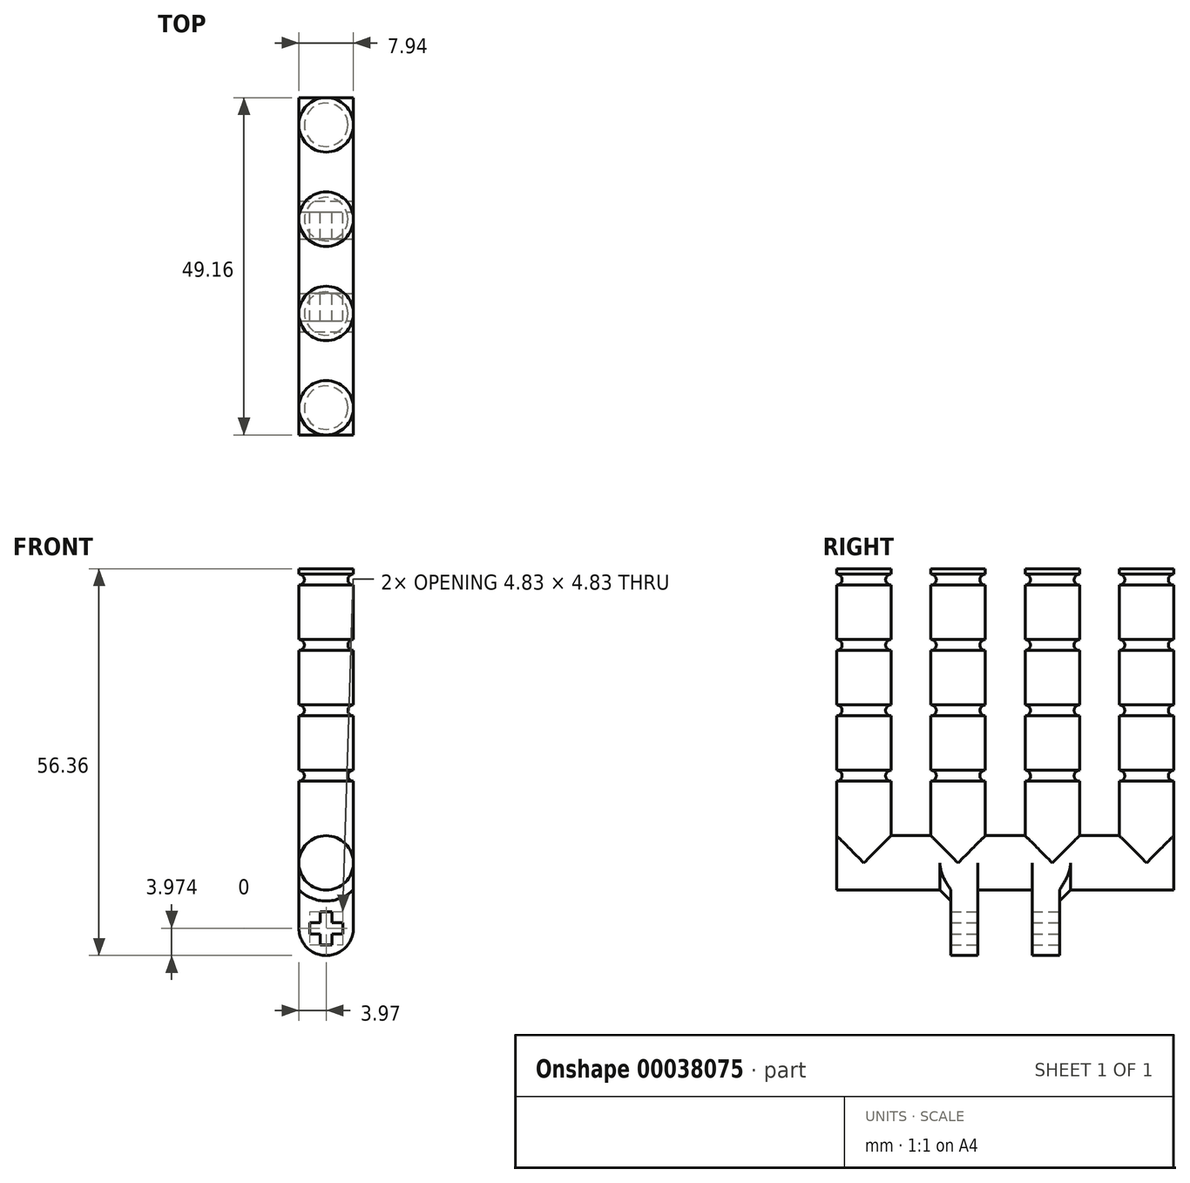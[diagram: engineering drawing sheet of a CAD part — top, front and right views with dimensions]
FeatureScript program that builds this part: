
annotation { "Feature Type Name" : "Feature", "Feature Type Description" : "" }
export const myFeature = defineFeature(function(context is Context, id is Id, definition is map)
    precondition{}
    {
        {
            var Q0;
            Q0=qCreatedBy(makeId("Top.planeOp"),FACE);
            var sketch = newSketch(context, id + "F0", { "sketchPlane" : qUnion([Q0])});
            skLineSegment(sketch, "E0.rect.bottom", {"start": v(3.97, -24.58) * mm, "end": v(-3.97, -24.58) * mm});
            skLineSegment(sketch, "E0.rect.top", {"start": v(3.97, 24.58) * mm, "end": v(-3.97, 24.58) * mm});
            skLineSegment(sketch, "E0.rect.left", {"start": v(3.97, -24.58) * mm, "end": v(3.97, 24.58) * mm});
            skLineSegment(sketch, "E0.rect.right", {"start": v(-3.97, -24.58) * mm, "end": v(-3.97, 24.58) * mm});
            skPoint(sketch, "E0.rect.middle", {"position": v(0, 0) * mm});
            skSolve(sketch);
        }
        {
            var Q0;
            Q0 = qSketchRegion(id + "F0", true);
            extrude(context, id + "F1", {"entities" : qUnion([Q0]), "depth" : 7.94 * mm});
        }
        {
            var Q0;
            Q0=makeQuery(id+"F1.opExtrude","CAP_FACE",FACE,{"disambiguationData":[OSD([sQuery(id+"F0.wireOp",EDGE,"E0.rect.bottom"),sQuery(id+"F0.wireOp",EDGE,"E0.rect.top"),sQuery(id+"F0.wireOp",EDGE,"E0.rect.left"),sQuery(id+"F0.wireOp",EDGE,"E0.rect.right")])],"isStart":false});
            var sketch = newSketch(context, id + "F2", { "sketchPlane" : qUnion([Q0])});
            skLineSegment(sketch, "E1", {"start": v(0, 24.58) * mm, "end": v(0, 20.61) * mm, "construction": true});
            skLineSegment(sketch, "E2", {"start": v(0, 20.61) * mm, "end": v(0, 6.87) * mm, "construction": true});
            skLineSegment(sketch, "E3", {"start": v(0, 6.87) * mm, "end": v(0, -6.87) * mm, "construction": true});
            skLineSegment(sketch, "E4", {"start": v(0, -6.87) * mm, "end": v(0, -20.61) * mm, "construction": true});
            skLineSegment(sketch, "E5", {"start": v(0, -20.61) * mm, "end": v(0, -24.58) * mm, "construction": true});
            skCircle(sketch, "E6", {"center": v(0, 20.61) * mm, "radius": 3.97 * mm});
            skCircle(sketch, "E7", {"center": v(0, -20.61) * mm, "radius": 3.97 * mm});
            skCircle(sketch, "E8", {"center": v(0, -6.87) * mm, "radius": 3.97 * mm});
            skCircle(sketch, "E9", {"center": v(0, 6.87) * mm, "radius": 3.97 * mm});
            skSolve(sketch);
        }
        {
            var Q0;
            Q0 = qSketchRegion(id + "F2", true);
            extrude(context, id + "F3", {"entities" : qUnion([Q0]), "operationType" : NewBodyOperationType.ADD, "depth" : 152.4 * mm});
        }
        {
            var Q0;
            Q0=makeQuery(id+"F1.opExtrude","CAP_FACE",FACE,{"disambiguationData":[OSD([sQuery(id+"F0.wireOp",EDGE,"E0.rect.bottom"),sQuery(id+"F0.wireOp",EDGE,"E0.rect.top"),sQuery(id+"F0.wireOp",EDGE,"E0.rect.left"),sQuery(id+"F0.wireOp",EDGE,"E0.rect.right")])],"isStart":true});
            var sketch = newSketch(context, id + "F4", { "sketchPlane" : qUnion([Q0])});
            skLineSegment(sketch, "E10", {"start": v(3.97, 0) * mm, "end": v(0, 0) * mm, "construction": true});
            skPoint(sketch, "E10.endSnap0", {"position": v(3.97, 0) * mm});
            skLineSegment(sketch, "E11", {"start": v(0, -3.97) * mm, "end": v(0, 3.97) * mm, "construction": true});
            skLineSegment(sketch, "E12.bottom", {"start": v(-3.97, 3.97) * mm, "end": v(3.97, 3.97) * mm});
            skLineSegment(sketch, "E12.top", {"start": v(-3.97, 7.94) * mm, "end": v(3.97, 7.94) * mm});
            skLineSegment(sketch, "E12.left", {"start": v(-3.97, 3.97) * mm, "end": v(-3.97, 7.94) * mm});
            skLineSegment(sketch, "E12.right", {"start": v(3.97, 3.97) * mm, "end": v(3.97, 7.94) * mm});
            skLineSegment(sketch, "E13.bottom", {"start": v(-3.97, -7.94) * mm, "end": v(3.97, -7.94) * mm});
            skLineSegment(sketch, "E13.top", {"start": v(-3.97, -3.97) * mm, "end": v(3.97, -3.97) * mm});
            skLineSegment(sketch, "E13.left", {"start": v(-3.97, -7.94) * mm, "end": v(-3.97, -3.97) * mm});
            skLineSegment(sketch, "E13.right", {"start": v(3.97, -7.94) * mm, "end": v(3.97, -3.97) * mm});
            skSolve(sketch);
        }
        {
            var Q0;
            Q0 = qSketchRegion(id + "F4", true);
            extrude(context, id + "F5", {"entities" : qUnion([Q0]), "operationType" : NewBodyOperationType.ADD, "depth" : 9.52 * mm});
        }
        {
            var Q0;
            Q0=qCreatedBy(makeId("Right.planeOp"),FACE);
            var sketch = newSketch(context, id + "F6", { "sketchPlane" : qUnion([Q0])});
            skLineSegment(sketch, "E14", {"start": v(24.58, 7.94) * mm, "end": v(24.58, 15.88) * mm});
            skLineSegment(sketch, "E15.bottom", {"start": v(24.58, 15.88) * mm, "end": v(23.79, 15.88) * mm});
            skLineSegment(sketch, "E15.top", {"start": v(24.58, 17.46) * mm, "end": v(23.79, 17.46) * mm});
            skLineSegment(sketch, "E15.left", {"start": v(24.58, 15.88) * mm, "end": v(24.58, 17.46) * mm});
            skLineSegment(sketch, "E15.right", {"start": v(23.79, 15.88) * mm, "end": v(23.79, 17.46) * mm, "construction": true});
            skLineSegment(sketch, "E16", {"start": v(24.58, 17.46) * mm, "end": v(24.58, 25.4) * mm, "construction": true});
            skLineSegment(sketch, "E17.bottom", {"start": v(24.58, 25.4) * mm, "end": v(23.79, 25.4) * mm});
            skLineSegment(sketch, "E17.top", {"start": v(24.58, 26.99) * mm, "end": v(23.79, 26.99) * mm});
            skLineSegment(sketch, "E17.left", {"start": v(24.58, 25.4) * mm, "end": v(24.58, 26.99) * mm});
            skLineSegment(sketch, "E17.right", {"start": v(23.79, 25.4) * mm, "end": v(23.79, 26.99) * mm, "construction": true});
            skLineSegment(sketch, "E18.bottom", {"start": v(24.58, 46.04) * mm, "end": v(23.79, 46.04) * mm});
            skLineSegment(sketch, "E18.top", {"start": v(24.58, 44.45) * mm, "end": v(23.79, 44.45) * mm});
            skLineSegment(sketch, "E18.left", {"start": v(24.58, 44.45) * mm, "end": v(24.58, 46.04) * mm});
            skLineSegment(sketch, "E18.right", {"start": v(23.79, 44.45) * mm, "end": v(23.79, 46.04) * mm, "construction": true});
            skLineSegment(sketch, "E19.bottom", {"start": v(24.58, 34.92) * mm, "end": v(23.79, 34.92) * mm});
            skLineSegment(sketch, "E19.top", {"start": v(24.58, 36.51) * mm, "end": v(23.79, 36.51) * mm});
            skLineSegment(sketch, "E19.left", {"start": v(24.58, 34.92) * mm, "end": v(24.58, 36.51) * mm});
            skLineSegment(sketch, "E19.right", {"start": v(23.79, 34.92) * mm, "end": v(23.79, 36.51) * mm, "construction": true});
            skLineSegment(sketch, "E20", {"start": v(24.58, 26.99) * mm, "end": v(24.58, 34.92) * mm, "construction": true});
            skLineSegment(sketch, "E21", {"start": v(24.58, 36.51) * mm, "end": v(24.58, 44.45) * mm, "construction": true});
            skArc(sketch, "E22", {"start": v(24.58, 17.46) * mm, "mid": v(23.79, 16.67) * mm, "end": v(24.58, 15.88) * mm});
            skArc(sketch, "E23", {"start": v(24.58, 26.99) * mm, "mid": v(23.79, 26.2) * mm, "end": v(24.58, 25.4) * mm});
            skArc(sketch, "E24", {"start": v(24.58, 36.51) * mm, "mid": v(23.79, 35.72) * mm, "end": v(24.58, 34.92) * mm});
            skArc(sketch, "E25", {"start": v(24.58, 46.04) * mm, "mid": v(23.79, 45.24) * mm, "end": v(24.58, 44.45) * mm});
            skLineSegment(sketch, "E26", {"start": v(24.58, 46.04) * mm, "end": v(24.58, 46.83) * mm});
            skLineSegment(sketch, "E27.bottom", {"start": v(24.58, 46.83) * mm, "end": v(20.61, 46.83) * mm});
            skLineSegment(sketch, "E27.top", {"start": v(24.58, 160.34) * mm, "end": v(20.61, 160.34) * mm});
            skLineSegment(sketch, "E27.left", {"start": v(24.58, 46.83) * mm, "end": v(24.58, 160.34) * mm});
            skLineSegment(sketch, "E27.right", {"start": v(20.61, 46.83) * mm, "end": v(20.61, 160.34) * mm});
            skSolve(sketch);
        }
        {
            var Q0;
            Q0 = qSketchRegion(id + "F6", true);
            var Q1;
            Q1=makeQuery(id+"F3.opExtrude","CAP_EDGE",EDGE,{"disambiguationData":[OSD([sQuery(id+"F2.wireOp",EDGE,"E6")])],"isStart":false});
            revolve(context, id + "F7", {"operationType" : NewBodyOperationType.REMOVE, "entities" : qUnion([Q0]), "axis" : qUnion([Q1]), "revolveType" : RevolveType.FULL, "oppositeDirection" : true});
        }
        {
            var Q0;
            Q0=qCreatedBy(makeId("Right.planeOp"),FACE);
            var sketch = newSketch(context, id + "F8", { "sketchPlane" : qUnion([Q0])});
            skLineSegment(sketch, "E28", {"start": v(10.84, 7.94) * mm, "end": v(6.87, 7.94) * mm, "construction": true});
            skLineSegment(sketch, "E29", {"start": v(10.84, 7.94) * mm, "end": v(10.84, 15.88) * mm, "construction": true});
            skLineSegment(sketch, "E30.bottom", {"start": v(10.84, 15.88) * mm, "end": v(10.05, 15.88) * mm, "construction": true});
            skLineSegment(sketch, "E30.top", {"start": v(10.84, 17.46) * mm, "end": v(10.05, 17.46) * mm, "construction": true});
            skLineSegment(sketch, "E30.left", {"start": v(10.84, 15.88) * mm, "end": v(10.84, 17.46) * mm});
            skLineSegment(sketch, "E30.right", {"start": v(10.05, 15.88) * mm, "end": v(10.05, 17.46) * mm, "construction": true});
            skLineSegment(sketch, "E31", {"start": v(10.84, 17.46) * mm, "end": v(10.84, 25.4) * mm, "construction": true});
            skLineSegment(sketch, "E32.bottom", {"start": v(10.84, 25.4) * mm, "end": v(10.05, 25.4) * mm, "construction": true});
            skLineSegment(sketch, "E32.top", {"start": v(10.84, 26.99) * mm, "end": v(10.05, 26.99) * mm, "construction": true});
            skLineSegment(sketch, "E32.left", {"start": v(10.84, 25.4) * mm, "end": v(10.84, 26.99) * mm});
            skLineSegment(sketch, "E32.right", {"start": v(10.05, 25.4) * mm, "end": v(10.05, 26.99) * mm, "construction": true});
            skArc(sketch, "E33", {"start": v(10.84, 26.99) * mm, "mid": v(10.05, 26.2) * mm, "end": v(10.84, 25.4) * mm});
            skArc(sketch, "E34", {"start": v(10.84, 17.46) * mm, "mid": v(10.05, 16.67) * mm, "end": v(10.84, 15.88) * mm});
            skLineSegment(sketch, "E35", {"start": v(10.84, 26.99) * mm, "end": v(10.84, 34.93) * mm, "construction": true});
            skLineSegment(sketch, "E36", {"start": v(10.84, 36.51) * mm, "end": v(10.84, 44.45) * mm, "construction": true});
            skLineSegment(sketch, "E37.bottom", {"start": v(10.84, 34.93) * mm, "end": v(10.05, 34.93) * mm, "construction": true});
            skLineSegment(sketch, "E37.top", {"start": v(10.84, 36.51) * mm, "end": v(10.05, 36.51) * mm, "construction": true});
            skLineSegment(sketch, "E37.left", {"start": v(10.84, 34.93) * mm, "end": v(10.84, 36.51) * mm});
            skLineSegment(sketch, "E37.right", {"start": v(10.05, 34.93) * mm, "end": v(10.05, 36.51) * mm, "construction": true});
            skLineSegment(sketch, "E38.bottom", {"start": v(10.84, 44.45) * mm, "end": v(10.05, 44.45) * mm, "construction": true});
            skLineSegment(sketch, "E38.top", {"start": v(10.84, 46.04) * mm, "end": v(10.05, 46.04) * mm, "construction": true});
            skLineSegment(sketch, "E38.left", {"start": v(10.84, 44.45) * mm, "end": v(10.84, 46.04) * mm});
            skLineSegment(sketch, "E38.right", {"start": v(10.05, 44.45) * mm, "end": v(10.05, 46.04) * mm, "construction": true});
            skLineSegment(sketch, "E39", {"start": v(10.84, 46.04) * mm, "end": v(10.84, 46.83) * mm});
            skLineSegment(sketch, "E40.bottom", {"start": v(10.84, 46.83) * mm, "end": v(6.87, 46.83) * mm});
            skLineSegment(sketch, "E40.top", {"start": v(10.84, 160.34) * mm, "end": v(6.87, 160.34) * mm});
            skLineSegment(sketch, "E40.left", {"start": v(10.84, 46.83) * mm, "end": v(10.84, 160.34) * mm});
            skLineSegment(sketch, "E40.right", {"start": v(6.87, 46.83) * mm, "end": v(6.87, 160.34) * mm});
            skArc(sketch, "E41", {"start": v(10.84, 46.04) * mm, "mid": v(10.05, 45.24) * mm, "end": v(10.84, 44.45) * mm});
            skArc(sketch, "E42", {"start": v(10.84, 36.51) * mm, "mid": v(10.05, 35.72) * mm, "end": v(10.84, 34.93) * mm});
            skSolve(sketch);
        }
        {
            var Q0;
            Q0 = qSketchRegion(id + "F8", true);
            var Q1;
            Q1=makeQuery(id+"F3.opExtrude","CAP_EDGE",EDGE,{"disambiguationData":[OSD([sQuery(id+"F2.wireOp",EDGE,"E9")])],"isStart":false});
            revolve(context, id + "F9", {"operationType" : NewBodyOperationType.REMOVE, "entities" : qUnion([Q0]), "axis" : qUnion([Q1]), "revolveType" : RevolveType.FULL, "oppositeDirection" : true});
        }
        {
            var Q0;
            Q0=qCreatedBy(makeId("Right.planeOp"),FACE);
            var sketch = newSketch(context, id + "F10", { "sketchPlane" : qUnion([Q0])});
            skLineSegment(sketch, "E43", {"start": v(-6.87, 7.94) * mm, "end": v(-2.9, 7.94) * mm});
            skLineSegment(sketch, "E44", {"start": v(-2.9, 7.94) * mm, "end": v(-2.9, 15.88) * mm, "construction": true});
            skLineSegment(sketch, "E45.bottom", {"start": v(-2.9, 15.88) * mm, "end": v(-3.7, 15.88) * mm});
            skLineSegment(sketch, "E45.top", {"start": v(-2.9, 17.46) * mm, "end": v(-3.7, 17.46) * mm});
            skLineSegment(sketch, "E45.left", {"start": v(-2.9, 15.88) * mm, "end": v(-2.9, 17.46) * mm});
            skLineSegment(sketch, "E45.right", {"start": v(-3.7, 15.88) * mm, "end": v(-3.7, 17.46) * mm, "construction": true});
            skLineSegment(sketch, "E46", {"start": v(-2.9, 17.46) * mm, "end": v(-2.9, 25.4) * mm, "construction": true});
            skLineSegment(sketch, "E47.bottom", {"start": v(-2.9, 25.4) * mm, "end": v(-3.7, 25.4) * mm});
            skLineSegment(sketch, "E47.top", {"start": v(-2.9, 26.99) * mm, "end": v(-3.7, 26.99) * mm});
            skLineSegment(sketch, "E47.left", {"start": v(-2.9, 25.4) * mm, "end": v(-2.9, 26.99) * mm});
            skLineSegment(sketch, "E47.right", {"start": v(-3.7, 25.4) * mm, "end": v(-3.7, 26.99) * mm, "construction": true});
            skLineSegment(sketch, "E48", {"start": v(-2.9, 26.99) * mm, "end": v(-2.9, 34.93) * mm, "construction": true});
            skLineSegment(sketch, "E49.bottom", {"start": v(-2.9, 34.93) * mm, "end": v(-3.7, 34.93) * mm});
            skLineSegment(sketch, "E49.top", {"start": v(-2.9, 36.51) * mm, "end": v(-3.7, 36.51) * mm, "construction": true});
            skLineSegment(sketch, "E49.left", {"start": v(-2.9, 34.93) * mm, "end": v(-2.9, 36.51) * mm});
            skLineSegment(sketch, "E49.right", {"start": v(-3.7, 34.93) * mm, "end": v(-3.7, 36.51) * mm, "construction": true});
            skLineSegment(sketch, "E50", {"start": v(-2.9, 36.51) * mm, "end": v(-2.9, 44.45) * mm, "construction": true});
            skLineSegment(sketch, "E51.bottom", {"start": v(-2.9, 44.45) * mm, "end": v(-3.7, 44.45) * mm});
            skLineSegment(sketch, "E51.top", {"start": v(-2.9, 46.04) * mm, "end": v(-3.7, 46.04) * mm, "construction": true});
            skLineSegment(sketch, "E51.left", {"start": v(-2.9, 44.45) * mm, "end": v(-2.9, 46.04) * mm});
            skLineSegment(sketch, "E51.right", {"start": v(-3.7, 44.45) * mm, "end": v(-3.7, 46.04) * mm, "construction": true});
            skLineSegment(sketch, "E52", {"start": v(-2.9, 46.04) * mm, "end": v(-2.9, 46.83) * mm, "construction": true});
            skLineSegment(sketch, "E53.bottom", {"start": v(-2.9, 46.83) * mm, "end": v(-6.87, 46.83) * mm});
            skLineSegment(sketch, "E53.top", {"start": v(-2.9, 160.34) * mm, "end": v(-6.87, 160.34) * mm});
            skLineSegment(sketch, "E53.left", {"start": v(-2.9, 46.83) * mm, "end": v(-2.9, 160.34) * mm});
            skLineSegment(sketch, "E53.right", {"start": v(-6.87, 46.83) * mm, "end": v(-6.87, 160.34) * mm});
            skArc(sketch, "E54", {"start": v(-2.9, 46.04) * mm, "mid": v(-3.7, 45.24) * mm, "end": v(-2.9, 44.45) * mm});
            skArc(sketch, "E55", {"start": v(-2.9, 36.51) * mm, "mid": v(-3.7, 35.72) * mm, "end": v(-2.9, 34.93) * mm});
            skArc(sketch, "E56", {"start": v(-2.9, 26.99) * mm, "mid": v(-3.7, 26.2) * mm, "end": v(-2.9, 25.4) * mm});
            skArc(sketch, "E57", {"start": v(-2.9, 17.46) * mm, "mid": v(-3.7, 16.67) * mm, "end": v(-2.9, 15.88) * mm});
            skSolve(sketch);
        }
        {
            var Q0;
            Q0 = qSketchRegion(id + "F10", true);
            var Q1;
            Q1=makeQuery(id+"F3.opExtrude","CAP_EDGE",EDGE,{"disambiguationData":[OSD([sQuery(id+"F2.wireOp",EDGE,"E8")])],"isStart":false});
            revolve(context, id + "F11", {"operationType" : NewBodyOperationType.REMOVE, "entities" : qUnion([Q0]), "axis" : qUnion([Q1]), "revolveType" : RevolveType.FULL, "oppositeDirection" : true});
        }
        {
            var Q0;
            Q0=qCreatedBy(makeId("Right.planeOp"),FACE);
            var sketch = newSketch(context, id + "F12", { "sketchPlane" : qUnion([Q0])});
            skLineSegment(sketch, "E58", {"start": v(-20.61, 7.94) * mm, "end": v(-16.64, 7.94) * mm});
            skLineSegment(sketch, "E59", {"start": v(-16.64, 7.94) * mm, "end": v(-16.64, 15.88) * mm, "construction": true});
            skLineSegment(sketch, "E60.bottom", {"start": v(-16.64, 15.88) * mm, "end": v(-17.44, 15.88) * mm});
            skLineSegment(sketch, "E60.top", {"start": v(-16.64, 17.46) * mm, "end": v(-17.44, 17.46) * mm, "construction": true});
            skLineSegment(sketch, "E60.left", {"start": v(-16.64, 15.88) * mm, "end": v(-16.64, 17.46) * mm});
            skLineSegment(sketch, "E60.right", {"start": v(-17.44, 15.88) * mm, "end": v(-17.44, 17.46) * mm, "construction": true});
            skLineSegment(sketch, "E61", {"start": v(-16.64, 17.46) * mm, "end": v(-16.64, 25.4) * mm, "construction": true});
            skLineSegment(sketch, "E62.bottom", {"start": v(-16.64, 25.4) * mm, "end": v(-17.44, 25.4) * mm});
            skLineSegment(sketch, "E62.top", {"start": v(-16.64, 26.99) * mm, "end": v(-17.44, 26.99) * mm, "construction": true});
            skLineSegment(sketch, "E62.left", {"start": v(-16.64, 25.4) * mm, "end": v(-16.64, 26.99) * mm});
            skLineSegment(sketch, "E62.right", {"start": v(-17.44, 25.4) * mm, "end": v(-17.44, 26.99) * mm, "construction": true});
            skLineSegment(sketch, "E63", {"start": v(-16.64, 26.99) * mm, "end": v(-16.64, 34.93) * mm, "construction": true});
            skLineSegment(sketch, "E64.bottom", {"start": v(-16.64, 34.93) * mm, "end": v(-17.44, 34.93) * mm});
            skLineSegment(sketch, "E64.top", {"start": v(-16.64, 36.51) * mm, "end": v(-17.44, 36.51) * mm, "construction": true});
            skLineSegment(sketch, "E64.left", {"start": v(-16.64, 34.93) * mm, "end": v(-16.64, 36.51) * mm});
            skLineSegment(sketch, "E64.right", {"start": v(-17.44, 34.93) * mm, "end": v(-17.44, 36.51) * mm, "construction": true});
            skLineSegment(sketch, "E65", {"start": v(-16.64, 36.51) * mm, "end": v(-16.64, 44.45) * mm, "construction": true});
            skLineSegment(sketch, "E66.bottom", {"start": v(-16.64, 44.45) * mm, "end": v(-17.44, 44.45) * mm, "construction": true});
            skLineSegment(sketch, "E66.top", {"start": v(-16.64, 46.04) * mm, "end": v(-17.44, 46.04) * mm});
            skLineSegment(sketch, "E66.left", {"start": v(-16.64, 44.45) * mm, "end": v(-16.64, 46.04) * mm});
            skLineSegment(sketch, "E66.right", {"start": v(-17.44, 44.45) * mm, "end": v(-17.44, 46.04) * mm, "construction": true});
            skArc(sketch, "E67", {"start": v(-16.64, 46.04) * mm, "mid": v(-17.44, 45.24) * mm, "end": v(-16.64, 44.45) * mm});
            skArc(sketch, "E68", {"start": v(-16.64, 36.51) * mm, "mid": v(-17.44, 35.72) * mm, "end": v(-16.64, 34.93) * mm});
            skArc(sketch, "E69", {"start": v(-16.64, 26.99) * mm, "mid": v(-17.44, 26.2) * mm, "end": v(-16.64, 25.4) * mm});
            skArc(sketch, "E70", {"start": v(-16.64, 17.46) * mm, "mid": v(-17.44, 16.67) * mm, "end": v(-16.64, 15.88) * mm});
            skLineSegment(sketch, "E71", {"start": v(-16.64, 46.04) * mm, "end": v(-16.64, 46.83) * mm, "construction": true});
            skLineSegment(sketch, "E72.bottom", {"start": v(-16.64, 46.83) * mm, "end": v(-20.61, 46.83) * mm});
            skLineSegment(sketch, "E72.top", {"start": v(-16.64, 160.34) * mm, "end": v(-20.61, 160.34) * mm});
            skLineSegment(sketch, "E72.left", {"start": v(-16.64, 46.83) * mm, "end": v(-16.64, 160.34) * mm});
            skLineSegment(sketch, "E72.right", {"start": v(-20.61, 46.83) * mm, "end": v(-20.61, 160.34) * mm});
            skSolve(sketch);
        }
        {
            var Q0;
            Q0 = qSketchRegion(id + "F12", true);
            var Q1;
            Q1=makeQuery(id+"F3.opExtrude","CAP_EDGE",EDGE,{"disambiguationData":[OSD([sQuery(id+"F2.wireOp",EDGE,"E7")])],"isStart":false});
            revolve(context, id + "F13", {"operationType" : NewBodyOperationType.REMOVE, "entities" : qUnion([Q0]), "axis" : qUnion([Q1]), "revolveType" : RevolveType.FULL, "oppositeDirection" : true});
        }
        {
            var Q0;
            {var subQ0=sQuery(id+"F0.wireOp",EDGE,"E0.rect.right");Q0=makeQuery(id+"F3.boolean.opBoolean","SPLIT",EDGE,{"disambiguationData":[TD([makeQuery(id+"F1.opExtrude","CAP_FACE",FACE,{"disambiguationData":[OSD([sQuery(id+"F0.wireOp",EDGE,"E0.rect.bottom"),sQuery(id+"F0.wireOp",EDGE,"E0.rect.top"),sQuery(id+"F0.wireOp",EDGE,"E0.rect.left"),subQ0])],"isStart":false}),makeQuery(id+"F1.opExtrude","SWEPT_FACE",FACE,{"disambiguationData":[OSD([subQ0])]}),makeQuery(id+"F3.opExtrude","SWEPT_FACE",FACE,{"disambiguationData":[OSD([sQuery(id+"F2.wireOp",EDGE,"E6")])]}),makeQuery(id+"F3.opExtrude","SWEPT_FACE",FACE,{"disambiguationData":[OSD([sQuery(id+"F2.wireOp",EDGE,"E9")])]})])],"derivedFrom":makeQuery(id+"F1.opExtrude","CAP_EDGE",EDGE,{"disambiguationData":[OSD([subQ0])],"isStart":false})});}
            var Q1;
            {var subQ0=sQuery(id+"F0.wireOp",EDGE,"E0.rect.right");Q1=makeQuery(id+"F3.boolean.opBoolean","SPLIT",EDGE,{"disambiguationData":[TD([makeQuery(id+"F1.opExtrude","CAP_FACE",FACE,{"disambiguationData":[OSD([sQuery(id+"F0.wireOp",EDGE,"E0.rect.bottom"),sQuery(id+"F0.wireOp",EDGE,"E0.rect.top"),sQuery(id+"F0.wireOp",EDGE,"E0.rect.left"),subQ0])],"isStart":false}),makeQuery(id+"F1.opExtrude","SWEPT_FACE",FACE,{"disambiguationData":[OSD([subQ0])]}),makeQuery(id+"F3.opExtrude","SWEPT_FACE",FACE,{"disambiguationData":[OSD([sQuery(id+"F2.wireOp",EDGE,"E8")])]}),makeQuery(id+"F3.opExtrude","SWEPT_FACE",FACE,{"disambiguationData":[OSD([sQuery(id+"F2.wireOp",EDGE,"E9")])]})])],"derivedFrom":makeQuery(id+"F1.opExtrude","CAP_EDGE",EDGE,{"disambiguationData":[OSD([subQ0])],"isStart":false})});}
            var Q2;
            {var subQ0=sQuery(id+"F0.wireOp",EDGE,"E0.rect.right");Q2=makeQuery(id+"F3.boolean.opBoolean","SPLIT",EDGE,{"disambiguationData":[TD([makeQuery(id+"F1.opExtrude","CAP_FACE",FACE,{"disambiguationData":[OSD([sQuery(id+"F0.wireOp",EDGE,"E0.rect.bottom"),sQuery(id+"F0.wireOp",EDGE,"E0.rect.top"),sQuery(id+"F0.wireOp",EDGE,"E0.rect.left"),subQ0])],"isStart":false}),makeQuery(id+"F1.opExtrude","SWEPT_FACE",FACE,{"disambiguationData":[OSD([subQ0])]}),makeQuery(id+"F3.opExtrude","SWEPT_FACE",FACE,{"disambiguationData":[OSD([sQuery(id+"F2.wireOp",EDGE,"E7")])]}),makeQuery(id+"F3.opExtrude","SWEPT_FACE",FACE,{"disambiguationData":[OSD([sQuery(id+"F2.wireOp",EDGE,"E8")])]})])],"derivedFrom":makeQuery(id+"F1.opExtrude","CAP_EDGE",EDGE,{"disambiguationData":[OSD([subQ0])],"isStart":false})});}
            var Q3;
            {var subQ0=sQuery(id+"F0.wireOp",EDGE,"E0.rect.right");var subQ1=sQuery(id+"F0.wireOp",EDGE,"E0.rect.top");Q3=makeQuery(id+"F3.boolean.opBoolean","SPLIT",EDGE,{"disambiguationData":[TD([makeQuery(id+"F1.opExtrude","CAP_FACE",FACE,{"disambiguationData":[OSD([sQuery(id+"F0.wireOp",EDGE,"E0.rect.bottom"),subQ1,sQuery(id+"F0.wireOp",EDGE,"E0.rect.left"),subQ0])],"isStart":false}),makeQuery(id+"F1.opExtrude","SWEPT_FACE",FACE,{"disambiguationData":[OSD([subQ1])]}),makeQuery(id+"F1.opExtrude","SWEPT_FACE",FACE,{"disambiguationData":[OSD([subQ0])]}),makeQuery(id+"F3.opExtrude","SWEPT_FACE",FACE,{"disambiguationData":[OSD([sQuery(id+"F2.wireOp",EDGE,"E6")])]})])],"derivedFrom":makeQuery(id+"F1.opExtrude","CAP_EDGE",EDGE,{"disambiguationData":[OSD([subQ0])],"isStart":false})});}
            var Q4;
            {var subQ0=sQuery(id+"F0.wireOp",EDGE,"E0.rect.bottom");var subQ1=sQuery(id+"F0.wireOp",EDGE,"E0.rect.right");Q4=makeQuery(id+"F3.boolean.opBoolean","SPLIT",EDGE,{"disambiguationData":[TD([makeQuery(id+"F1.opExtrude","SWEPT_FACE",FACE,{"disambiguationData":[OSD([subQ0])]}),makeQuery(id+"F1.opExtrude","CAP_FACE",FACE,{"disambiguationData":[OSD([subQ0,sQuery(id+"F0.wireOp",EDGE,"E0.rect.top"),sQuery(id+"F0.wireOp",EDGE,"E0.rect.left"),subQ1])],"isStart":false}),makeQuery(id+"F1.opExtrude","SWEPT_FACE",FACE,{"disambiguationData":[OSD([subQ1])]}),makeQuery(id+"F3.opExtrude","SWEPT_FACE",FACE,{"disambiguationData":[OSD([sQuery(id+"F2.wireOp",EDGE,"E7")])]})])],"derivedFrom":makeQuery(id+"F1.opExtrude","CAP_EDGE",EDGE,{"disambiguationData":[OSD([subQ1])],"isStart":false})});}
            var Q5;
            {var subQ0=sQuery(id+"F0.wireOp",EDGE,"E0.rect.right");var subQ1=sQuery(id+"F0.wireOp",EDGE,"E0.rect.bottom");Q5=makeQuery(id+"F5.boolean.opBoolean","SPLIT",EDGE,{"disambiguationData":[TD([makeQuery(id+"F1.opExtrude","SWEPT_FACE",FACE,{"disambiguationData":[OSD([subQ1])]})])],"derivedFrom":makeQuery(id+"F1.opExtrude","CAP_EDGE",EDGE,{"disambiguationData":[OSD([subQ0])],"isStart":true})});}
            var Q6;
            {var subQ0=sQuery(id+"F0.wireOp",EDGE,"E0.rect.right");Q6=makeQuery(id+"F5.boolean.opBoolean","SPLIT",EDGE,{"disambiguationData":[TD([makeQuery(id+"F5.opExtrude","SWEPT_FACE",FACE,{"disambiguationData":[OSD([sQuery(id+"F4.wireOp",EDGE,"E12.bottom")])]})])],"derivedFrom":makeQuery(id+"F1.opExtrude","CAP_EDGE",EDGE,{"disambiguationData":[OSD([subQ0])],"isStart":true})});}
            var Q7;
            {var subQ0=sQuery(id+"F0.wireOp",EDGE,"E0.rect.right");var subQ1=sQuery(id+"F0.wireOp",EDGE,"E0.rect.top");Q7=makeQuery(id+"F5.boolean.opBoolean","SPLIT",EDGE,{"disambiguationData":[TD([makeQuery(id+"F1.opExtrude","SWEPT_FACE",FACE,{"disambiguationData":[OSD([subQ1])]})])],"derivedFrom":makeQuery(id+"F1.opExtrude","CAP_EDGE",EDGE,{"disambiguationData":[OSD([subQ0])],"isStart":true})});}
            var Q8;
            {var subQ0=sQuery(id+"F0.wireOp",EDGE,"E0.rect.left");Q8=makeQuery(id+"F3.boolean.opBoolean","SPLIT",EDGE,{"disambiguationData":[TD([makeQuery(id+"F1.opExtrude","CAP_FACE",FACE,{"disambiguationData":[OSD([sQuery(id+"F0.wireOp",EDGE,"E0.rect.bottom"),sQuery(id+"F0.wireOp",EDGE,"E0.rect.top"),subQ0,sQuery(id+"F0.wireOp",EDGE,"E0.rect.right")])],"isStart":false}),makeQuery(id+"F1.opExtrude","SWEPT_FACE",FACE,{"disambiguationData":[OSD([subQ0])]}),makeQuery(id+"F3.opExtrude","SWEPT_FACE",FACE,{"disambiguationData":[OSD([sQuery(id+"F2.wireOp",EDGE,"E6")])]}),makeQuery(id+"F3.opExtrude","SWEPT_FACE",FACE,{"disambiguationData":[OSD([sQuery(id+"F2.wireOp",EDGE,"E9")])]})])],"derivedFrom":makeQuery(id+"F1.opExtrude","CAP_EDGE",EDGE,{"disambiguationData":[OSD([subQ0])],"isStart":false})});}
            var Q9;
            {var subQ0=sQuery(id+"F0.wireOp",EDGE,"E0.rect.left");var subQ1=sQuery(id+"F0.wireOp",EDGE,"E0.rect.top");Q9=makeQuery(id+"F3.boolean.opBoolean","SPLIT",EDGE,{"disambiguationData":[TD([makeQuery(id+"F1.opExtrude","CAP_FACE",FACE,{"disambiguationData":[OSD([sQuery(id+"F0.wireOp",EDGE,"E0.rect.bottom"),subQ1,subQ0,sQuery(id+"F0.wireOp",EDGE,"E0.rect.right")])],"isStart":false}),makeQuery(id+"F1.opExtrude","SWEPT_FACE",FACE,{"disambiguationData":[OSD([subQ1])]}),makeQuery(id+"F1.opExtrude","SWEPT_FACE",FACE,{"disambiguationData":[OSD([subQ0])]}),makeQuery(id+"F3.opExtrude","SWEPT_FACE",FACE,{"disambiguationData":[OSD([sQuery(id+"F2.wireOp",EDGE,"E6")])]})])],"derivedFrom":makeQuery(id+"F1.opExtrude","CAP_EDGE",EDGE,{"disambiguationData":[OSD([subQ0])],"isStart":false})});}
            var Q10;
            {var subQ0=sQuery(id+"F0.wireOp",EDGE,"E0.rect.left");Q10=makeQuery(id+"F5.boolean.opBoolean","SPLIT",EDGE,{"disambiguationData":[TD([makeQuery(id+"F5.opExtrude","SWEPT_FACE",FACE,{"disambiguationData":[OSD([sQuery(id+"F4.wireOp",EDGE,"E12.bottom")])]})])],"derivedFrom":makeQuery(id+"F1.opExtrude","CAP_EDGE",EDGE,{"disambiguationData":[OSD([subQ0])],"isStart":true})});}
            var Q11;
            {var subQ0=sQuery(id+"F0.wireOp",EDGE,"E0.rect.left");var subQ1=sQuery(id+"F0.wireOp",EDGE,"E0.rect.top");Q11=makeQuery(id+"F5.boolean.opBoolean","SPLIT",EDGE,{"disambiguationData":[TD([makeQuery(id+"F1.opExtrude","SWEPT_FACE",FACE,{"disambiguationData":[OSD([subQ1])]})])],"derivedFrom":makeQuery(id+"F1.opExtrude","CAP_EDGE",EDGE,{"disambiguationData":[OSD([subQ0])],"isStart":true})});}
            var Q12;
            {var subQ0=sQuery(id+"F0.wireOp",EDGE,"E0.rect.left");Q12=makeQuery(id+"F3.boolean.opBoolean","SPLIT",EDGE,{"disambiguationData":[TD([makeQuery(id+"F1.opExtrude","CAP_FACE",FACE,{"disambiguationData":[OSD([sQuery(id+"F0.wireOp",EDGE,"E0.rect.bottom"),sQuery(id+"F0.wireOp",EDGE,"E0.rect.top"),subQ0,sQuery(id+"F0.wireOp",EDGE,"E0.rect.right")])],"isStart":false}),makeQuery(id+"F1.opExtrude","SWEPT_FACE",FACE,{"disambiguationData":[OSD([subQ0])]}),makeQuery(id+"F3.opExtrude","SWEPT_FACE",FACE,{"disambiguationData":[OSD([sQuery(id+"F2.wireOp",EDGE,"E8")])]}),makeQuery(id+"F3.opExtrude","SWEPT_FACE",FACE,{"disambiguationData":[OSD([sQuery(id+"F2.wireOp",EDGE,"E9")])]})])],"derivedFrom":makeQuery(id+"F1.opExtrude","CAP_EDGE",EDGE,{"disambiguationData":[OSD([subQ0])],"isStart":false})});}
            var Q13;
            {var subQ0=sQuery(id+"F0.wireOp",EDGE,"E0.rect.left");Q13=makeQuery(id+"F3.boolean.opBoolean","SPLIT",EDGE,{"disambiguationData":[TD([makeQuery(id+"F1.opExtrude","CAP_FACE",FACE,{"disambiguationData":[OSD([sQuery(id+"F0.wireOp",EDGE,"E0.rect.bottom"),sQuery(id+"F0.wireOp",EDGE,"E0.rect.top"),subQ0,sQuery(id+"F0.wireOp",EDGE,"E0.rect.right")])],"isStart":false}),makeQuery(id+"F1.opExtrude","SWEPT_FACE",FACE,{"disambiguationData":[OSD([subQ0])]}),makeQuery(id+"F3.opExtrude","SWEPT_FACE",FACE,{"disambiguationData":[OSD([sQuery(id+"F2.wireOp",EDGE,"E7")])]}),makeQuery(id+"F3.opExtrude","SWEPT_FACE",FACE,{"disambiguationData":[OSD([sQuery(id+"F2.wireOp",EDGE,"E8")])]})])],"derivedFrom":makeQuery(id+"F1.opExtrude","CAP_EDGE",EDGE,{"disambiguationData":[OSD([subQ0])],"isStart":false})});}
            var Q14;
            {var subQ0=sQuery(id+"F0.wireOp",EDGE,"E0.rect.left");var subQ1=sQuery(id+"F0.wireOp",EDGE,"E0.rect.bottom");Q14=makeQuery(id+"F5.boolean.opBoolean","SPLIT",EDGE,{"disambiguationData":[TD([makeQuery(id+"F1.opExtrude","SWEPT_FACE",FACE,{"disambiguationData":[OSD([subQ1])]})])],"derivedFrom":makeQuery(id+"F1.opExtrude","CAP_EDGE",EDGE,{"disambiguationData":[OSD([subQ0])],"isStart":true})});}
            var Q15;
            Q15=makeQuery(id+"F5.opExtrude","CAP_EDGE",EDGE,{"disambiguationData":[OSD([sQuery(id+"F4.wireOp",EDGE,"E12.right")])],"isStart":false});
            var Q16;
            Q16=makeQuery(id+"F5.opExtrude","CAP_EDGE",EDGE,{"disambiguationData":[OSD([sQuery(id+"F4.wireOp",EDGE,"E12.left")])],"isStart":false});
            var Q17;
            Q17=makeQuery(id+"F5.opExtrude","CAP_EDGE",EDGE,{"disambiguationData":[OSD([sQuery(id+"F4.wireOp",EDGE,"E13.left")])],"isStart":false});
            var Q18;
            Q18=makeQuery(id+"F5.opExtrude","CAP_EDGE",EDGE,{"disambiguationData":[OSD([sQuery(id+"F4.wireOp",EDGE,"E13.right")])],"isStart":false});
            fillet(context, id + "F14", {"entities" : qUnion([Q0, Q1, Q2, Q3, Q4, Q5, Q6, Q7, Q8, Q9, Q10, Q11, Q12, Q13, Q14, Q15, Q16, Q17, Q18]), "radius" : 3.97 * mm, "tangentPropagation" : true, "allowEdgeOverflow" : false});
        }
        {
            var Q0;
            {var subQ0=makeQuery(id+"F5.opExtrude","SWEPT_FACE",FACE,{"disambiguationData":[OSD([sQuery(id+"F4.wireOp",EDGE,"E13.bottom")])]});var subQ1=sQuery(id+"F0.wireOp",EDGE,"E0.rect.left");var subQ2=sQuery(id+"F0.wireOp",EDGE,"E0.rect.top");Q0=makeQuery(id+"F14.opFillet","BLEND_EDGE",EDGE,{"blendedFrom":[makeQuery(id+"F5.boolean.opBoolean","SPLIT",EDGE,{"disambiguationData":[TD([makeQuery(id+"F1.opExtrude","SWEPT_FACE",FACE,{"disambiguationData":[OSD([subQ2])]})])],"derivedFrom":makeQuery(id+"F1.opExtrude","CAP_EDGE",EDGE,{"disambiguationData":[OSD([subQ1])],"isStart":true})}),subQ0],"blendedInto":[subQ0]});}
            var Q1;
            {var subQ0=makeQuery(id+"F5.opExtrude","SWEPT_FACE",FACE,{"disambiguationData":[OSD([sQuery(id+"F4.wireOp",EDGE,"E12.top")])]});var subQ1=sQuery(id+"F0.wireOp",EDGE,"E0.rect.left");var subQ2=sQuery(id+"F0.wireOp",EDGE,"E0.rect.bottom");Q1=makeQuery(id+"F14.opFillet","BLEND_EDGE",EDGE,{"blendedFrom":[makeQuery(id+"F5.boolean.opBoolean","SPLIT",EDGE,{"disambiguationData":[TD([makeQuery(id+"F1.opExtrude","SWEPT_FACE",FACE,{"disambiguationData":[OSD([subQ2])]})])],"derivedFrom":makeQuery(id+"F1.opExtrude","CAP_EDGE",EDGE,{"disambiguationData":[OSD([subQ1])],"isStart":true})}),subQ0],"blendedInto":[subQ0]});}
            chamfer(context, id + "F15", {"entities" : qUnion([Q0, Q1]), "width" : 1.59 * mm, "tangentPropagation" : true});
        }
        {
            var Q0;
            Q0=makeQuery(id+"F5.opExtrude","SWEPT_FACE",FACE,{"disambiguationData":[OSD([sQuery(id+"F4.wireOp",EDGE,"E13.bottom")])]});
            var sketch = newSketch(context, id + "F16", { "sketchPlane" : qUnion([Q0])});
            skLineSegment(sketch, "E73.rect.bottom", {"start": v(2.41, -6.4) * mm, "end": v(-2.41, -6.4) * mm});
            skLineSegment(sketch, "E73.rect.top", {"start": v(2.41, -4.71) * mm, "end": v(-2.41, -4.71) * mm});
            skLineSegment(sketch, "E73.rect.left", {"start": v(2.41, -6.4) * mm, "end": v(2.41, -4.71) * mm});
            skLineSegment(sketch, "E73.rect.right", {"start": v(-2.41, -6.4) * mm, "end": v(-2.41, -4.71) * mm});
            skPoint(sketch, "E73.rect.middle", {"position": v(0, -5.56) * mm});
            skLineSegment(sketch, "E74.rect.bottom", {"start": v(0.84, -7.97) * mm, "end": v(-0.84, -7.97) * mm});
            skLineSegment(sketch, "E74.rect.top", {"start": v(0.84, -3.14) * mm, "end": v(-0.84, -3.14) * mm});
            skLineSegment(sketch, "E74.rect.left", {"start": v(0.84, -7.97) * mm, "end": v(0.84, -3.14) * mm});
            skLineSegment(sketch, "E74.rect.right", {"start": v(-0.84, -7.97) * mm, "end": v(-0.84, -3.14) * mm});
            skSolve(sketch);
        }
        {
            var Q0;
            Q0 = qSketchRegion(id + "F16", true);
            var Q1;
            Q1=makeQuery(id+"F5.opExtrude","SWEPT_FACE",FACE,{"disambiguationData":[OSD([sQuery(id+"F4.wireOp",EDGE,"E12.top")])]});
            extrude(context, id + "F17", {"entities" : qUnion([Q0]), "operationType" : NewBodyOperationType.REMOVE, "endBound" : BoundingType.UP_TO_SURFACE, "oppositeDirection" : true, "endBoundEntityFace" : qUnion([Q1]), "depth" : 25.4 * mm});
        }
    });
